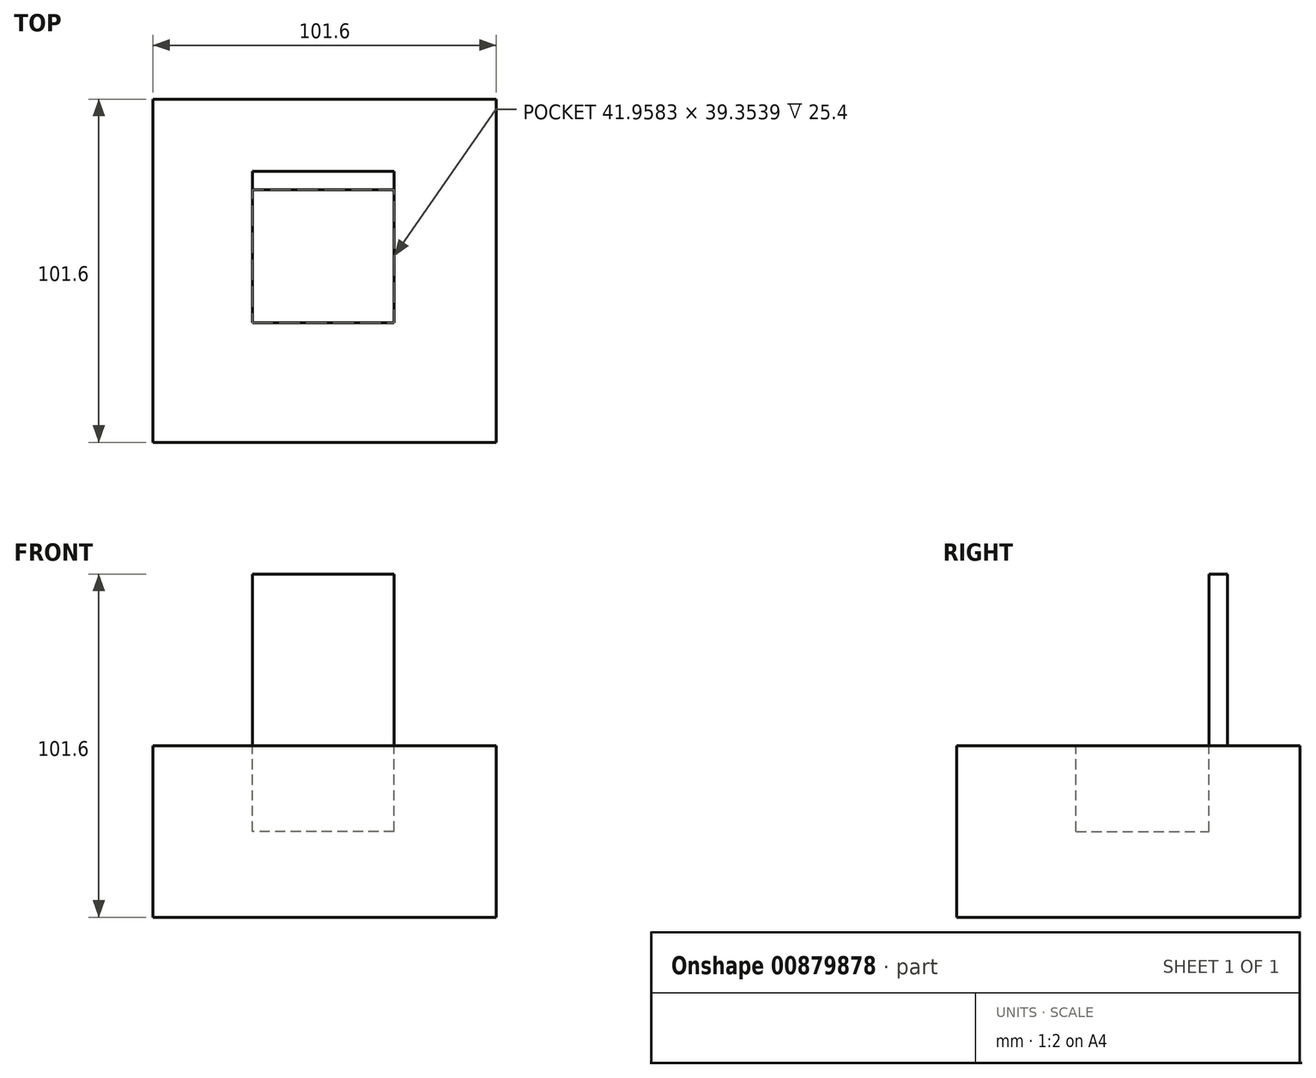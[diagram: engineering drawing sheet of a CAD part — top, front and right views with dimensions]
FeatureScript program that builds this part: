
annotation { "Feature Type Name" : "Feature", "Feature Type Description" : "" }
export const myFeature = defineFeature(function(context is Context, id is Id, definition is map)
    precondition{}
    {
        {
            var Q0;
            Q0=qCreatedBy(makeId("Top.planeOp"),FACE);
            var sketch = newSketch(context, id + "F0", { "sketchPlane" : qUnion([Q0])});
            skLineSegment(sketch, "E0", {"start": v(-52.72, 61.03) * mm, "end": v(48.88, 61.03) * mm});
            skLineSegment(sketch, "E1", {"start": v(-52.72, 61.03) * mm, "end": v(-52.72, -40.57) * mm});
            skLineSegment(sketch, "E2", {"start": v(-52.72, -40.57) * mm, "end": v(48.88, -40.57) * mm});
            skLineSegment(sketch, "E3", {"start": v(48.88, -40.57) * mm, "end": v(48.88, 61.03) * mm});
            skSolve(sketch);
        }
        {
            var Q0;
            Q0 = qSketchRegion(id + "F0", true);
            extrude(context, id + "F1", {"entities" : qUnion([Q0]), "depth" : 50.8 * mm, "offsetDistance" : 25.4 * mm});
        }
        {
            var Q0;
            Q0=makeQuery(id+"F1.opExtrude","CAP_FACE",FACE,{"disambiguationData":[OSD([sQuery(id+"F0.wireOp",EDGE,"E0"),sQuery(id+"F0.wireOp",EDGE,"E1"),sQuery(id+"F0.wireOp",EDGE,"E2"),sQuery(id+"F0.wireOp",EDGE,"E3")])],"isStart":false});
            var sketch = newSketch(context, id + "F2", { "sketchPlane" : qUnion([Q0])});
            skLineSegment(sketch, "E4.bottom", {"start": v(18.66, -5.2) * mm, "end": v(-23.3, -5.2) * mm});
            skLineSegment(sketch, "E4.top", {"start": v(18.66, 34.15) * mm, "end": v(-23.3, 34.15) * mm});
            skLineSegment(sketch, "E4.left", {"start": v(18.66, -5.2) * mm, "end": v(18.66, 34.15) * mm});
            skLineSegment(sketch, "E4.right", {"start": v(-23.3, -5.2) * mm, "end": v(-23.3, 34.15) * mm});
            skSolve(sketch);
        }
        {
            var Q0;
            Q0 = qSketchRegion(id + "F2", true);
            extrude(context, id + "F3", {"entities" : qUnion([Q0]), "operationType" : NewBodyOperationType.REMOVE, "oppositeDirection" : true, "depth" : 25.4 * mm, "offsetDistance" : 25.4 * mm});
        }
        {
            var Q0;
            Q0=makeQuery(id+"F1.opExtrude","CAP_FACE",FACE,{"disambiguationData":[OSD([sQuery(id+"F0.wireOp",EDGE,"E0"),sQuery(id+"F0.wireOp",EDGE,"E1"),sQuery(id+"F0.wireOp",EDGE,"E2"),sQuery(id+"F0.wireOp",EDGE,"E3")])],"isStart":false});
            var sketch = newSketch(context, id + "F4", { "sketchPlane" : qUnion([Q0])});
            skLineSegment(sketch, "E5", {"start": v(-23.3, 34.15) * mm, "end": v(-23.3, 39.64) * mm});
            skLineSegment(sketch, "E6", {"start": v(-23.3, 39.64) * mm, "end": v(18.66, 39.64) * mm});
            skLineSegment(sketch, "E7", {"start": v(18.66, 39.64) * mm, "end": v(18.66, 34.15) * mm});
            skLineSegment(sketch, "E8", {"start": v(18.66, 34.15) * mm, "end": v(-23.3, 34.15) * mm});
            skSolve(sketch);
        }
        {
            var Q0;
            Q0 = qSketchRegion(id + "F4", true);
            extrude(context, id + "F5", {"entities" : qUnion([Q0]), "operationType" : NewBodyOperationType.ADD, "depth" : 50.8 * mm, "offsetDistance" : 25.4 * mm});
        }
    });
